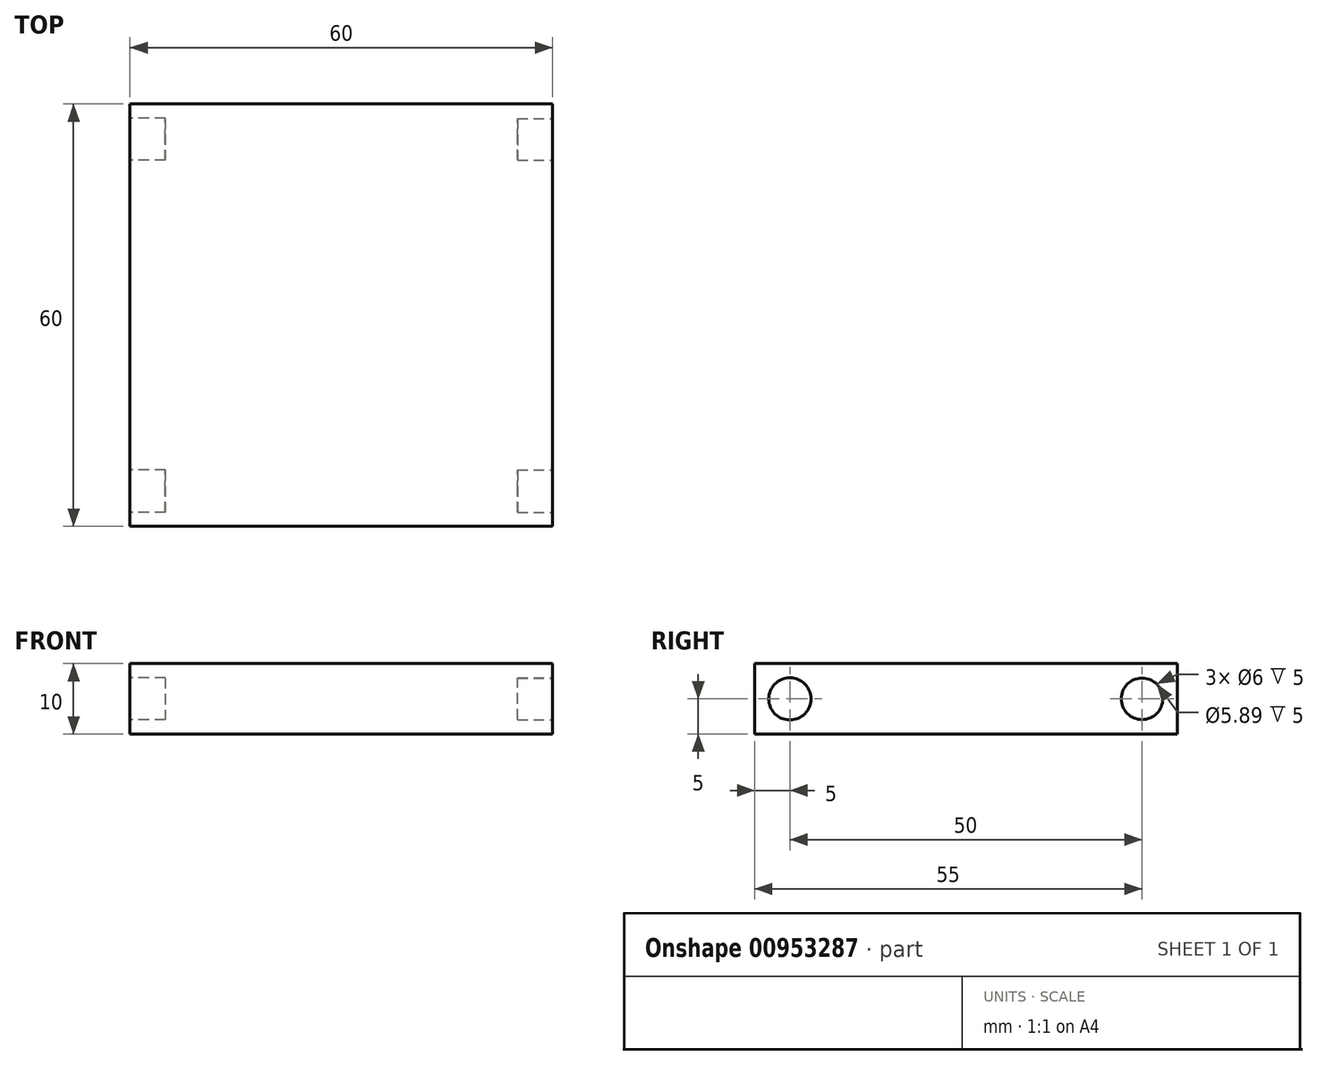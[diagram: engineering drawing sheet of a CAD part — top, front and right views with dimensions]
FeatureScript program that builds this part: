
annotation { "Feature Type Name" : "Feature", "Feature Type Description" : "" }
export const myFeature = defineFeature(function(context is Context, id is Id, definition is map)
    precondition{}
    {
        {
            var Q0;
            Q0=qCreatedBy(makeId("Top.planeOp"),FACE);
            var sketch = newSketch(context, id + "F0", { "sketchPlane" : qUnion([Q0])});
            skLineSegment(sketch, "E0.bottom", {"start": v(-30, 30) * mm, "end": v(30, 30) * mm});
            skLineSegment(sketch, "E0.top", {"start": v(-30, -30) * mm, "end": v(30, -30) * mm});
            skLineSegment(sketch, "E0.left", {"start": v(-30, 30) * mm, "end": v(-30, -30) * mm});
            skLineSegment(sketch, "E0.right", {"start": v(30, 30) * mm, "end": v(30, -30) * mm});
            skSolve(sketch);
        }
        {
            var Q0;
            Q0 = qSketchRegion(id + "F0", true);
            extrude(context, id + "F1", {"entities" : qUnion([Q0]), "depth" : 10 * mm, "offsetDistance" : 25 * mm});
        }
        {
            var Q0;
            Q0=makeQuery(id+"F1.opExtrude","SWEPT_FACE",FACE,{"disambiguationData":[OSD([sQuery(id+"F0.wireOp",EDGE,"E0.right")])]});
            var sketch = newSketch(context, id + "F2", { "sketchPlane" : qUnion([Q0])});
            skCircle(sketch, "E1", {"center": v(-25, 5) * mm, "radius": 3 * mm});
            skCircle(sketch, "E2", {"center": v(25, 5) * mm, "radius": 2.94 * mm});
            skSolve(sketch);
        }
        {
            var Q0;
            Q0=makeQuery(id+"F1.opExtrude","SWEPT_FACE",FACE,{"disambiguationData":[OSD([sQuery(id+"F0.wireOp",EDGE,"E0.left")])]});
            var sketch = newSketch(context, id + "F3", { "sketchPlane" : qUnion([Q0])});
            skCircle(sketch, "E3", {"center": v(-25, 5) * mm, "radius": 3 * mm});
            skCircle(sketch, "E4", {"center": v(25, 5) * mm, "radius": 3 * mm});
            skSolve(sketch);
        }
        {
            var Q0;
            Q0 = qSketchRegion(id + "F2", true);
            extrude(context, id + "F4", {"entities" : qUnion([Q0]), "operationType" : NewBodyOperationType.REMOVE, "oppositeDirection" : true, "depth" : 5 * mm, "offsetDistance" : 25 * mm});
        }
        {
            var Q0;
            Q0 = qSketchRegion(id + "F3", true);
            extrude(context, id + "F5", {"entities" : qUnion([Q0]), "operationType" : NewBodyOperationType.REMOVE, "oppositeDirection" : true, "depth" : 5 * mm, "offsetDistance" : 25 * mm});
        }
    });
